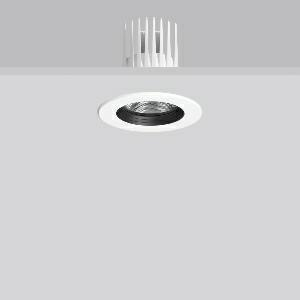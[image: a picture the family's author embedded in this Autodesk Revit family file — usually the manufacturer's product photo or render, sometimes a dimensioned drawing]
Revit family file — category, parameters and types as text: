
# Revit family: heledon_mini_e_901740_002_2_bb23
name_source: partatom
category: Lighting Fixtures
units: mm (PartAtom-declared; Revit-internal decimal feet)

## family parameters
Cut with Voids When Loaded = No
Host = Face
Light Source = No
Part Type = Normal
Room Calculation Point = No
Round Connector Dimension = Use Diameter
Shared = No

## types (1)
- HELEDON mini E (1 x LED Modul 927, 2400 lm, 2700)
    Apparent Load = 20 VA
    Approval mark = CE
    CIE Flux Codes = 100 100 100 100 100
    Color Rendering = 92
    Color Temperature = 2700
    Default Elevation = 1800 mm
    Description = Series: HELEDON mini
Round recessed downlight. Housing: die-cast aluminium, powder-coated. Black plastic ring and recessed LED to prevent glare from the side. Optical assembly with reflector made of MIRO-Silver with 98% total light reflection for outstanding efficiency - can be changed without tools. Best colour rendering index Ra>90. Suitable for Recessed ceiling mounting. Installation without tools thanks to spring fastening system. Including separate LED converter with connecting cable 600 mm.High quality converter without flickering and stroboscopic effect. Through-wiring box (5 pole) available as accessory. The following accessories can be mounted without use of tools: interchangeable lenses, decorative glasses, honeycomb louvre, clear and frosted diffusers, white interchangeable plastic ring. 
Colour: traffic white, matt (RAL 9016)
Diameter: 124 mm
Height: 3 mm
Cut-out diameter: 114 mm
Recess height: 170 mm
Luminaire: recess height: 120 mm
Lamp: LED
Socket: without socket
Colour temperature: 2700K
Colour rendering index (CRI): 92
System power: 20 W
Rated luminous flux: 2400 lm
Luminous efficiency: 120 lm/W
Control gear: Regulated power supply
Protection class: II
Type of protection: IP 20
    Height = 0 mm  [stored 0 ft]
    Lamp = 1 x LED Modul 927
    Lamp Light Flux = 2400 lm
    Lamp count = 1
    Length = 124 mm  [stored 0.406824 ft]
    Lifetime = 50000 h
    Luminous efficacy = 120 lm/W
    Manufacturer = RZB
    ModVariant = No
    Model = 901740.002.2
    Mounting Place = Ceiling
    Mounting Type = Recessed
    Number of Poles = 1
    OnlyDefault = Yes
    Power Factor = 1
    Product Name = HELEDON mini E
    Product group = Recessed downlights
    ProductGroupID = 402
    Protection Class = Protection class II
    Protection Degree = IP 20
    RLX_Detail_Level = 1
    RLX_Emergency_Light_Flux = 0 lm
    RLX_Emergency_Type = 0
    RLX_Emergency_Type_DB = No
    RlxData = <blob elided: 125861 chars, md5=880fc931>
    Socket = socket
    Standby Power = 0 W
    System Light Flux = 2400 lm
    System Power = 20 W
    Type Comments = Product without accessories
    Type Image = 901657.002.jpg
    URL = http://relux.com
    VarID = ---
    Voltage = 230 V
    Voltage Range = 220-240 V
    Weight = 0.00 kg
    Width = 0 mm  [stored 0 ft]

note: [stored X ft] marks values corroborated as IEEE doubles in the binary element streams (Revit-internal decimal feet)

## geometry (parser evidence)
native form markers: Blend x4, Sweep x12
no freeform markers — native parametric forms only
